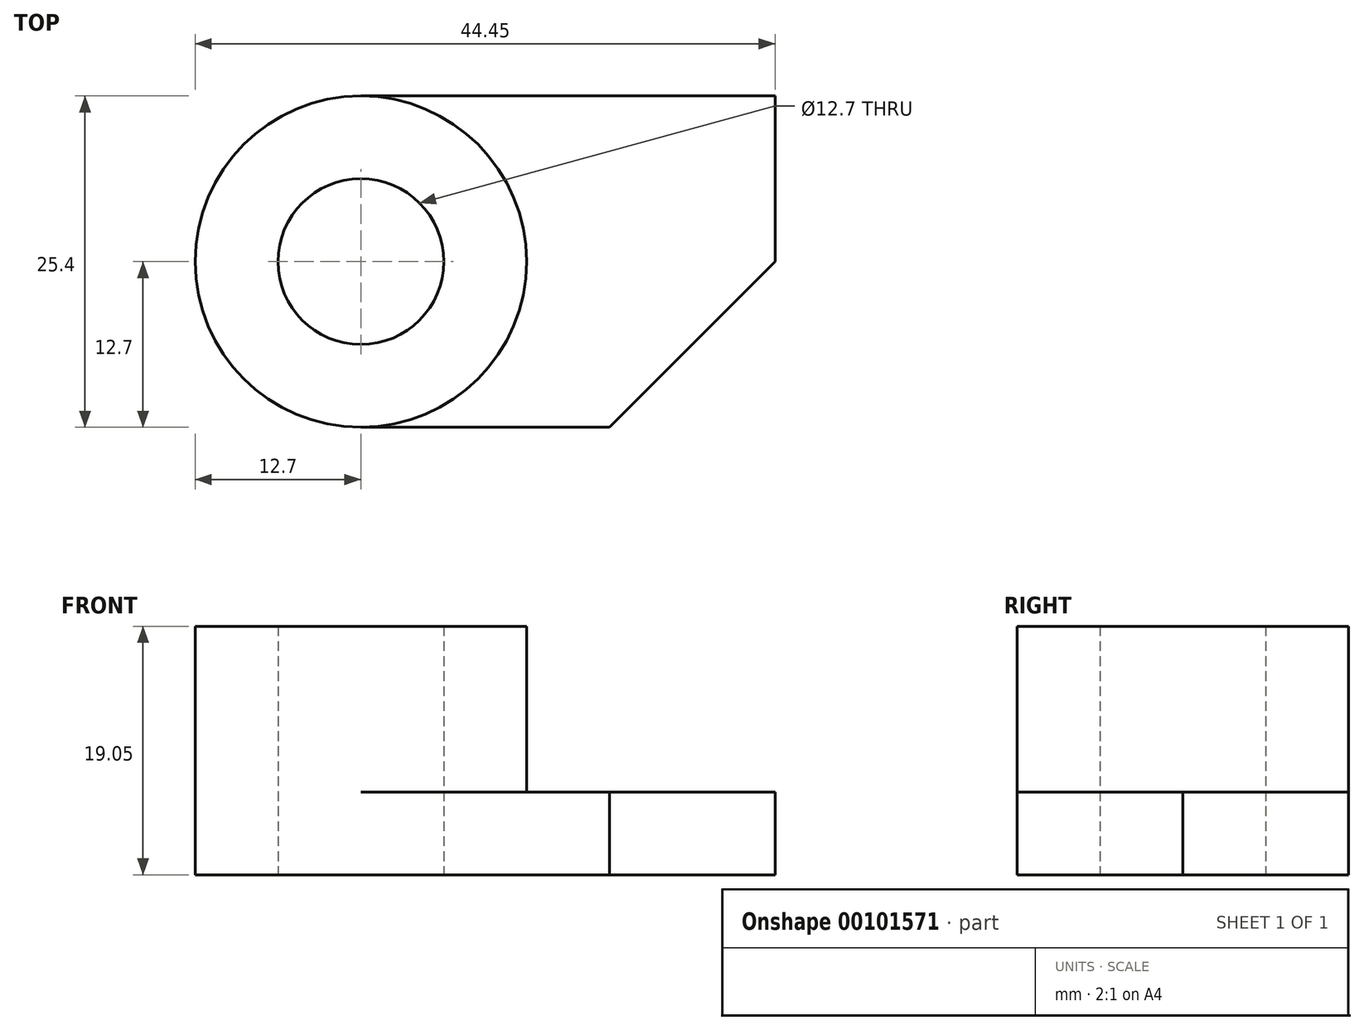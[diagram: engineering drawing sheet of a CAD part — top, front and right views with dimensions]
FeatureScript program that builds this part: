
annotation { "Feature Type Name" : "Feature", "Feature Type Description" : "" }
export const myFeature = defineFeature(function(context is Context, id is Id, definition is map)
    precondition{}
    {
        {
            var Q0;
            Q0=qCreatedBy(makeId("Top.planeOp"),FACE);
            var sketch = newSketch(context, id + "F0", { "sketchPlane" : qUnion([Q0])});
            skLineSegment(sketch, "E0.bottom", {"start": v(0, 0) * mm, "end": v(44.45, 0) * mm});
            skLineSegment(sketch, "E0.top", {"start": v(0, -25.4) * mm, "end": v(44.45, -25.4) * mm});
            skLineSegment(sketch, "E0.left", {"start": v(0, 0) * mm, "end": v(0, -25.4) * mm});
            skLineSegment(sketch, "E0.right", {"start": v(44.45, 0) * mm, "end": v(44.45, -25.4) * mm});
            skPoint(sketch, "E1", {"position": v(12.7, -12.7) * mm});
            skPoint(sketch, "E1.positionSnap0", {"position": v(0, -12.7) * mm});
            skCircle(sketch, "E2", {"center": v(12.7, -12.7) * mm, "radius": 6.35 * mm});
            skCircle(sketch, "E3", {"center": v(12.7, -12.7) * mm, "radius": 12.7 * mm});
            skSolve(sketch);
        }
        {
            var Q0;
            {var subQ0=sQuery(id+"F0.wireOp",EDGE,"E0.right");Q0=makeQuery(id+"F0.imprint","IMPRINT",FACE,{"disambiguationData":[TD([[makeQuery(id+"F0.imprint","IMPRINT",EDGE,{"derivedFrom":subQ0}),-1.0]])]});}
            extrude(context, id + "F1", {"entities" : qUnion([Q0]), "depth" : 6.35 * mm});
        }
        {
            var Q0;
            Q0=makeQuery(id+"F0.imprint","IMPRINT",FACE,{"disambiguationData":[TD([[makeQuery(id+"F0.imprint","IMPRINT",EDGE,{"derivedFrom":sQuery(id+"F0.wireOp",EDGE,"E2")}),-1.0]])]});
            extrude(context, id + "F2", {"entities" : qUnion([Q0]), "operationType" : NewBodyOperationType.ADD, "depth" : 19.05 * mm});
        }
        {
            var Q0;
            Q0=qCreatedBy(makeId("Top.planeOp"),FACE);
            var sketch = newSketch(context, id + "F3", { "sketchPlane" : qUnion([Q0])});
            skLineSegment(sketch, "E4", {"start": v(31.75, -25.4) * mm, "end": v(44.45, -12.7) * mm});
            skLineSegment(sketch, "E5", {"start": v(44.45, -12.7) * mm, "end": v(44.45, -25.4) * mm});
            skLineSegment(sketch, "E6", {"start": v(44.45, -25.4) * mm, "end": v(31.75, -25.4) * mm});
            skSolve(sketch);
        }
        {
            var Q0;
            Q0 = qSketchRegion(id + "F3", true);
            extrude(context, id + "F4", {"entities" : qUnion([Q0]), "operationType" : NewBodyOperationType.REMOVE, "endBound" : BoundingType.THROUGH_ALL, "depth" : 25.4 * mm});
        }
    });
